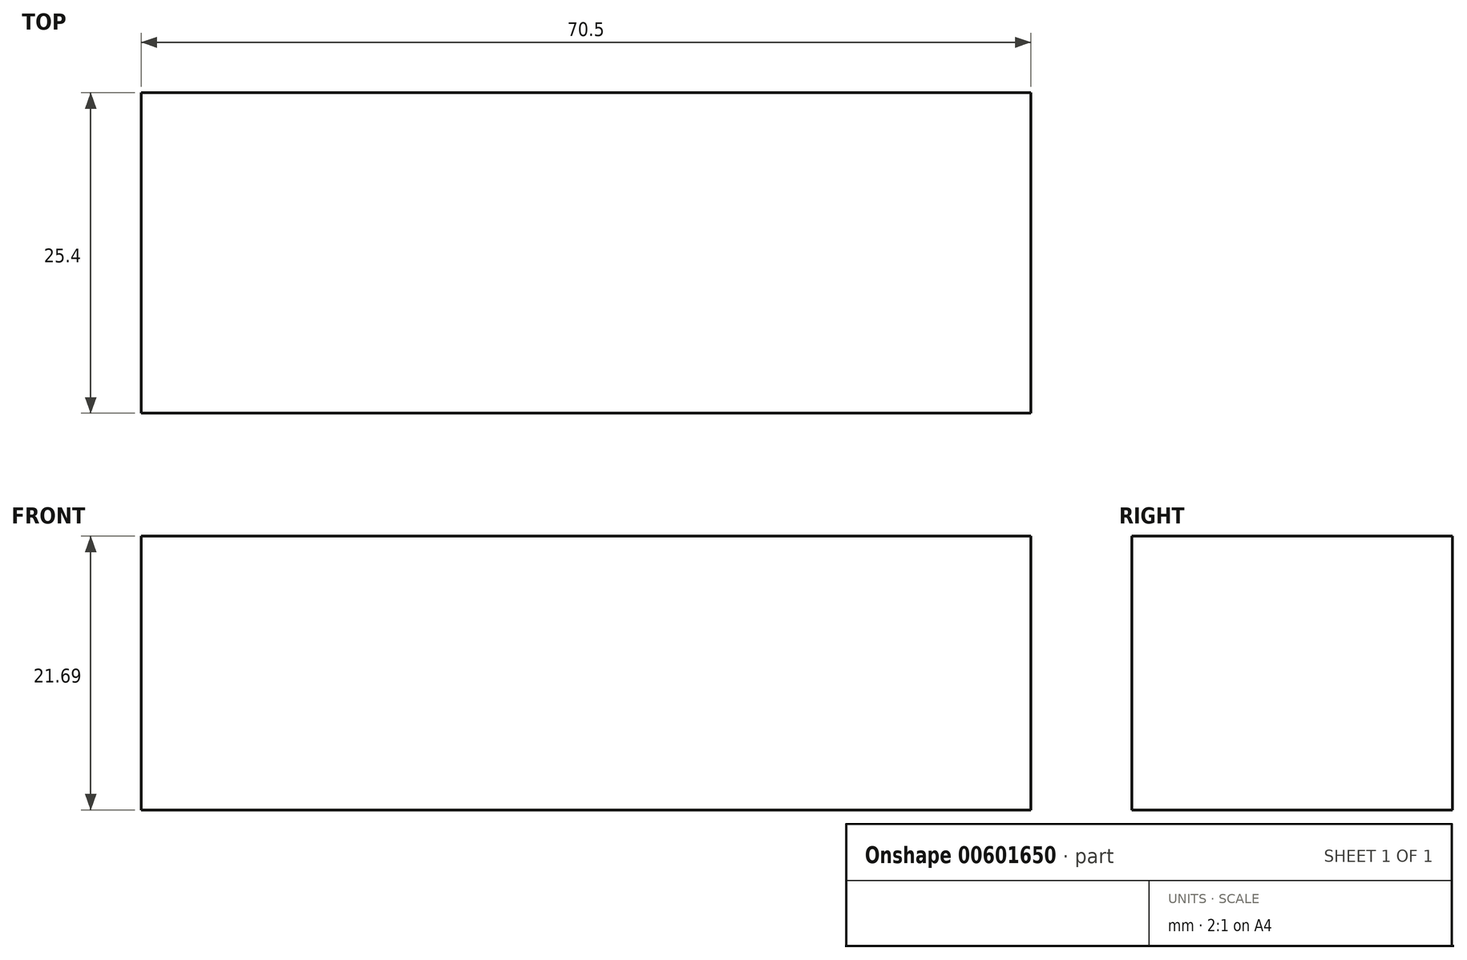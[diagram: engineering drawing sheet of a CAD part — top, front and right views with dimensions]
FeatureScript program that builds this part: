
annotation { "Feature Type Name" : "Feature", "Feature Type Description" : "" }
export const myFeature = defineFeature(function(context is Context, id is Id, definition is map)
    precondition{}
    {
        {
            var Q0;
            Q0=qCreatedBy(makeId("Front.planeOp"),FACE);
            var sketch = newSketch(context, id + "F0", { "sketchPlane" : qUnion([Q0])});
            skLineSegment(sketch, "E0.bottom", {"start": v(0, -2.84) * mm, "end": v(-70.5, -2.84) * mm});
            skLineSegment(sketch, "E0.top", {"start": v(0, 18.85) * mm, "end": v(-70.5, 18.85) * mm});
            skLineSegment(sketch, "E0.left", {"start": v(0, -2.84) * mm, "end": v(0, 18.85) * mm});
            skLineSegment(sketch, "E0.right", {"start": v(-70.5, -2.84) * mm, "end": v(-70.5, 18.85) * mm});
            skSolve(sketch);
        }
        {
            var Q0;
            Q0 = qSketchRegion(id + "F0", true);
            extrude(context, id + "F1", {"entities" : qUnion([Q0]), "depth" : 25.4 * mm, "offsetDistance" : 25.4 * mm});
        }
    });
